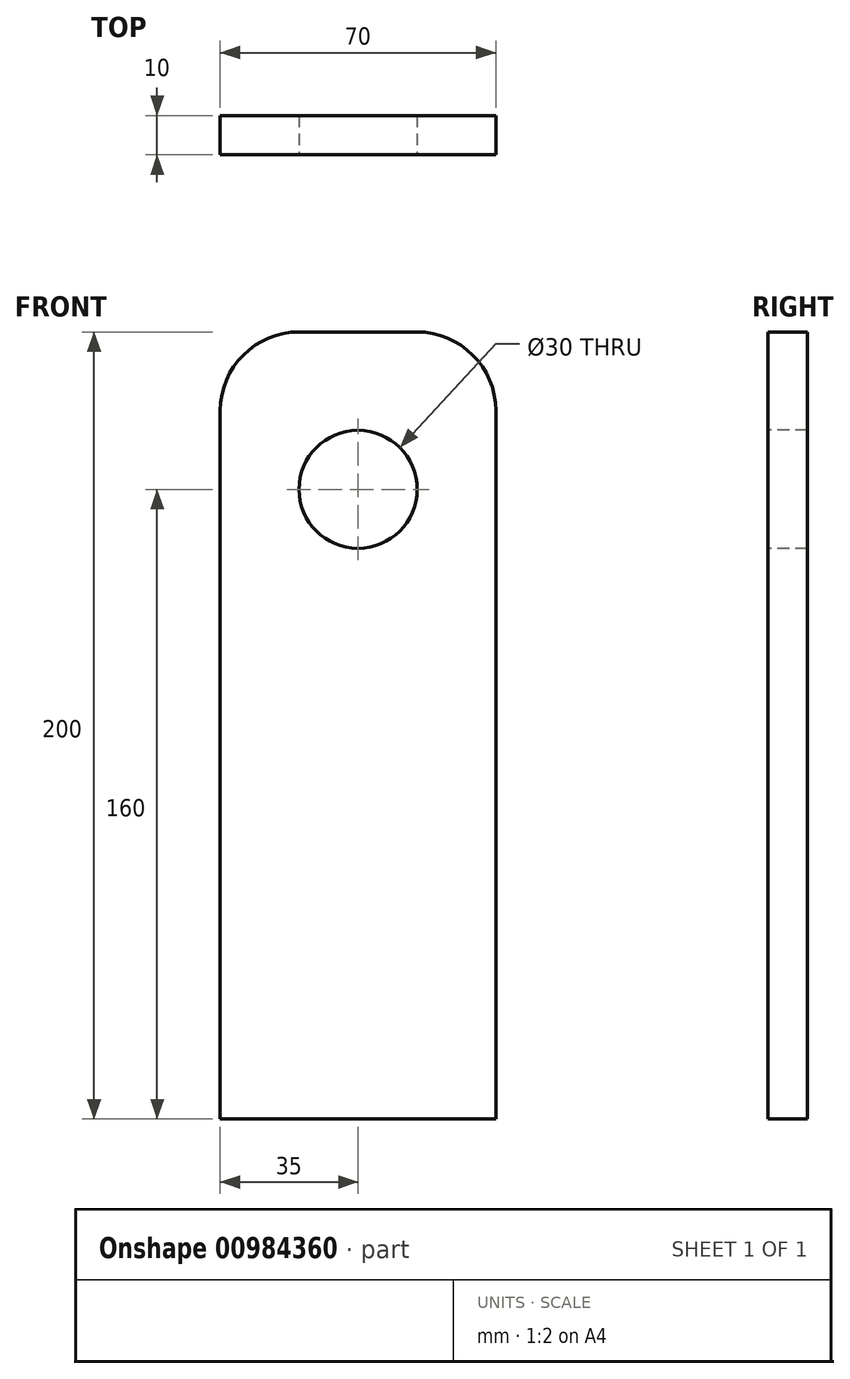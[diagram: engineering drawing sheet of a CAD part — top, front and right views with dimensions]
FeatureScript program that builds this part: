
annotation { "Feature Type Name" : "Feature", "Feature Type Description" : "" }
export const myFeature = defineFeature(function(context is Context, id is Id, definition is map)
    precondition{}
    {
        {
            var Q0;
            Q0=qCreatedBy(makeId("Front.planeOp"),FACE);
            var sketch = newSketch(context, id + "F0", { "sketchPlane" : qUnion([Q0])});
            skLineSegment(sketch, "E0.bottom", {"start": v(35, -100) * mm, "end": v(-35, -100) * mm});
            skLineSegment(sketch, "E0.top", {"start": v(35, 100) * mm, "end": v(-35, 100) * mm});
            skLineSegment(sketch, "E0.left", {"start": v(35, -100) * mm, "end": v(35, 100) * mm});
            skLineSegment(sketch, "E0.right", {"start": v(-35, -100) * mm, "end": v(-35, 100) * mm});
            skPoint(sketch, "E0.middle", {"position": v(0, 0) * mm});
            skSolve(sketch);
        }
        {
            var Q0;
            Q0=qSketchRegion(id+"F0",true);
            extrude(context, id + "F1", {"entities" : qUnion([Q0]), "depth" : 10 * mm, "offsetDistance" : 25 * mm});
        }
        {
            var Q0;
            Q0=qCreatedBy(makeId("Front.planeOp"),FACE);
            var sketch = newSketch(context, id + "F2", { "sketchPlane" : qUnion([Q0])});
            skCircle(sketch, "E1", {"center": v(0, 60) * mm, "radius": 15 * mm});
            skSolve(sketch);
        }
        {
            var Q0;
            Q0=qSketchRegion(id+"F2",true);
            extrude(context, id + "F3", {"entities" : qUnion([Q0]), "operationType" : NewBodyOperationType.REMOVE, "endBound" : BoundingType.THROUGH_ALL, "oppositeDirection" : true, "depth" : 25 * mm, "offsetDistance" : 25 * mm, "hasSecondDirection" : true, "secondDirectionOppositeDirection" : false, "secondDirectionDepth" : 25 * mm});
        }
        {
            var Q0;
            Q0=makeQuery(id+"F1.opExtrude","SWEPT_EDGE",EDGE,{"disambiguationData":[OSD([sQuery(id+"F0.wireOp",EDGE,"E0.top"),sQuery(id+"F0.wireOp",EDGE,"E0.right")])]});
            var Q1;
            Q1=makeQuery(id+"F1.opExtrude","SWEPT_EDGE",EDGE,{"disambiguationData":[OSD([sQuery(id+"F0.wireOp",EDGE,"E0.top"),sQuery(id+"F0.wireOp",EDGE,"E0.left")])]});
            fillet(context, id + "F4", {"entities" : qUnion([Q0, Q1]), "radius" : 20 * mm, "tangentPropagation" : true, "allowEdgeOverflow" : false});
        }
    });
